# Revit family: ITK_Шина заземления_Непосредственная установка
name_source: partatom
category: Обобщенные модели
units: mm (PartAtom-declared; Revit-internal decimal feet)

## family parameters
Всегда вертикально = Да
Может служить основой для арматурных стержней = Нет
На основе рабочей плоскости = Нет
Общий = Нет
При загрузке вырезать с полостями = Нет
Размер круглого соединителя = Использовать диаметр
Тип детали = Нормальный
Точка расчета площади = Нет

## types (2) — shared parameters
ADSK_URL страницы изделия = https://www.itk-group.ru
ADSK_Версия Revit = 2019
ADSK_Версия семейства = 1.0
ADSK_Группирование = I. ЩИТЫ И ПУЛЬТЫ
ADSK_Единица измерения = компл
ADSK_Завод-изготовитель = IEK
ADSK_Материал наименование = Металл
ADSK_Наименование = ITK Набор закладных винтов-шайб-гаек M6x15мм (1 компл)
IEK_URL = https://www.itk-group.ru
IEK_Описание = Совместимы со всеми 19" шкафами и стойками ITK.
Удобны в монтаже и эксплуатации.
Винты имеют резьбу М6.
Соответствие российским и международным стандартам.
Поставляются в полиэтиленовом пакете.
KSI_CMa_Строительные материалы = 10.2.01.03
KSI_CPr_Строительные изделия = 01.7.15.04
URL = https://www.iek.ru
Изготовитель = ITK

## per-type parameters (varying)
| type | ADSK_Масса | IEK_Цена за единицу |
| ITK-HP-15 | 0.191 | 11.14 |
| ITK-HP-28 | 0.156667 | 10.72 |

note: column(s) folded — value = type name in every type: ADSK_Код изделия
